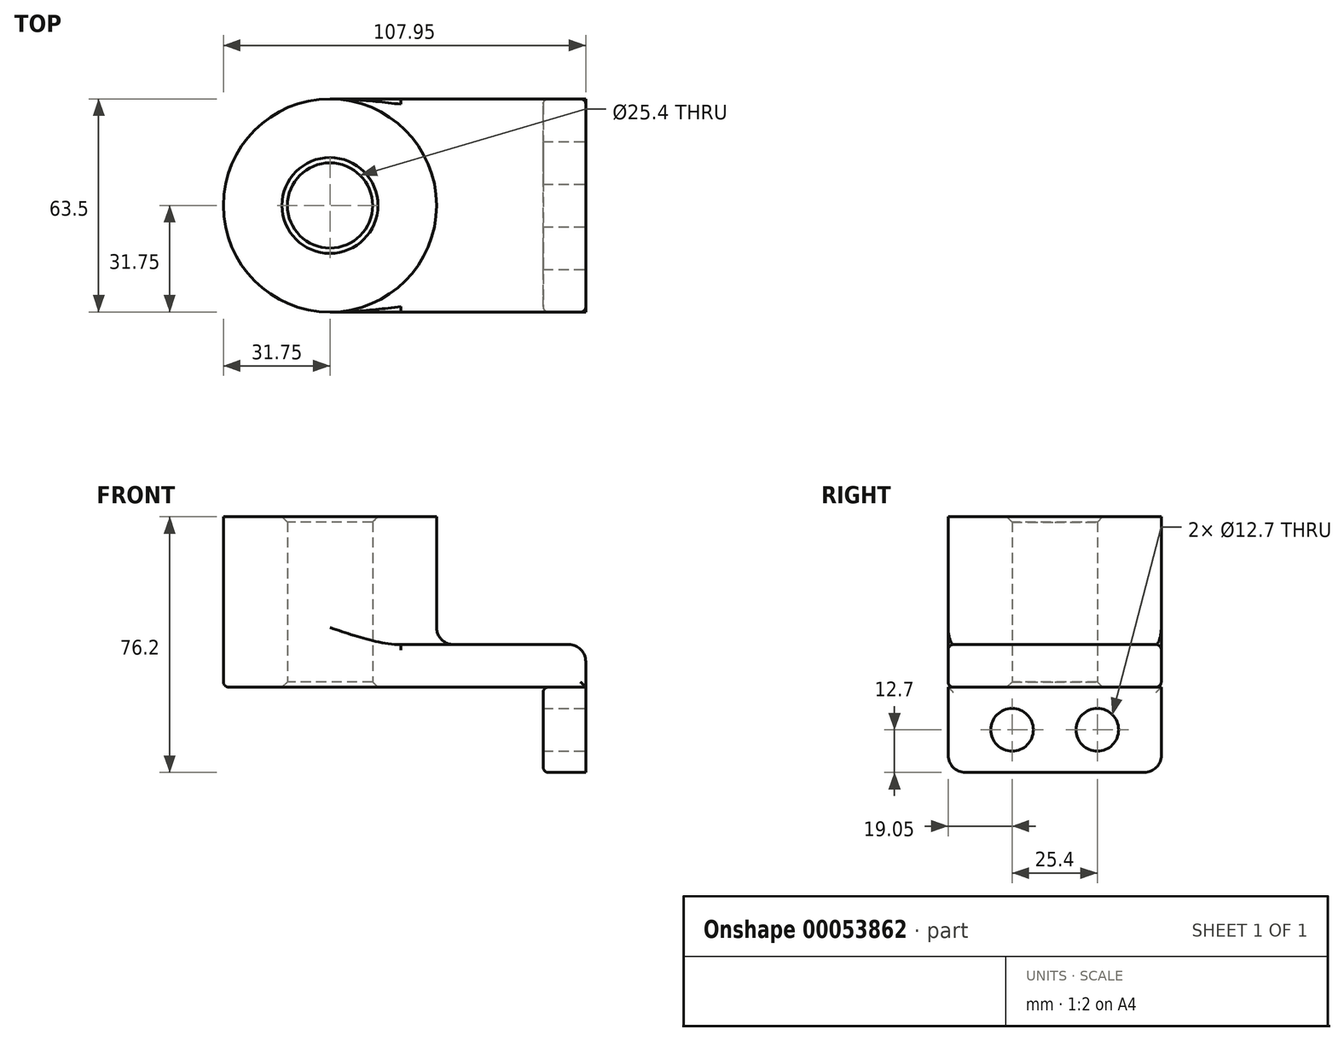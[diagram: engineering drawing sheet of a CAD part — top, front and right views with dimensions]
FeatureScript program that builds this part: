
annotation { "Feature Type Name" : "Feature", "Feature Type Description" : "" }
export const myFeature = defineFeature(function(context is Context, id is Id, definition is map)
    precondition{}
    {
        {
            var Q0;
            Q0=qCreatedBy(makeId("Top.planeOp"),FACE);
            var sketch = newSketch(context, id + "F0", { "sketchPlane" : qUnion([Q0])});
            skLineSegment(sketch, "E0.rect.bottom", {"start": v(-38.1, 31.75) * mm, "end": v(38.1, 31.75) * mm});
            skLineSegment(sketch, "E0.rect.top", {"start": v(-38.1, -31.75) * mm, "end": v(38.1, -31.75) * mm});
            skLineSegment(sketch, "E0.rect.left", {"start": v(-38.1, 31.75) * mm, "end": v(-38.1, -31.75) * mm});
            skLineSegment(sketch, "E0.rect.right", {"start": v(38.1, 31.75) * mm, "end": v(38.1, -31.75) * mm});
            skPoint(sketch, "E0.rect.middle", {"position": v(0, 0) * mm});
            skCircle(sketch, "E1", {"center": v(-38.1, 0) * mm, "radius": 31.75 * mm});
            skCircle(sketch, "E2", {"center": v(-38.1, 0) * mm, "radius": 12.7 * mm});
            skSolve(sketch);
        }
        {
            var Q0;
            Q0 = qSketchRegion(id + "F0", true);
            extrude(context, id + "F1", {"entities" : qUnion([Q0]), "depth" : 12.7 * mm});
        }
        {
            var Q0;
            {var subQ1=sQuery(id+"F0.wireOp",EDGE,"E0.rect.left");var subQ3=sQuery(id+"F0.wireOp",EDGE,"E2");var subQ4=makeQuery(id+"F0.imprint","INTERSECT",VERTEX,{"disambiguationData":[OD(0.0)],"derivedFrom":[subQ1,subQ3]});Q0=makeQuery(id+"F0.imprint","IMPRINT",FACE,{"disambiguationData":[TD([[makeQuery(id+"F0.imprint","IMPRINT",EDGE,{"disambiguationData":[TD([[subQ4,-1.0]])],"derivedFrom":subQ3}),-1.0]])]});}
            var Q1;
            {var subQ1=sQuery(id+"F0.wireOp",EDGE,"E0.rect.left");var subQ3=sQuery(id+"F0.wireOp",EDGE,"E2");var subQ4=makeQuery(id+"F0.imprint","INTERSECT",VERTEX,{"disambiguationData":[OD(0.0)],"derivedFrom":[subQ1,subQ3]});Q1=makeQuery(id+"F0.imprint","IMPRINT",FACE,{"disambiguationData":[TD([[makeQuery(id+"F0.imprint","IMPRINT",EDGE,{"disambiguationData":[TD([[subQ4,1.0]])],"derivedFrom":subQ3}),-1.0]])]});}
            extrude(context, id + "F2", {"entities" : qUnion([Q0, Q1]), "operationType" : NewBodyOperationType.ADD, "depth" : 50.8 * mm});
        }
        {
            var Q0;
            Q0=makeQuery(id+"F1.opExtrude","SWEPT_FACE",FACE,{"disambiguationData":[OSD([sQuery(id+"F0.wireOp",EDGE,"E0.rect.right")])]});
            var sketch = newSketch(context, id + "F3", { "sketchPlane" : qUnion([Q0])});
            skLineSegment(sketch, "E3.bottom", {"start": v(-31.75, 12.7) * mm, "end": v(31.75, 12.7) * mm});
            skLineSegment(sketch, "E3.top", {"start": v(-31.75, -25.4) * mm, "end": v(31.75, -25.4) * mm});
            skLineSegment(sketch, "E3.left", {"start": v(-31.75, 12.7) * mm, "end": v(-31.75, -25.4) * mm});
            skLineSegment(sketch, "E3.right", {"start": v(31.75, 12.7) * mm, "end": v(31.75, -25.4) * mm});
            skCircle(sketch, "E4", {"center": v(-12.7, -12.7) * mm, "radius": 6.35 * mm});
            skLineSegment(sketch, "E5", {"start": v(0, 0) * mm, "end": v(0, -25.4) * mm, "construction": true});
            skCircle(sketch, "E6.MirrorC", {"center": v(12.7, -12.7) * mm, "radius": 6.35 * mm});
            skSolve(sketch);
        }
        {
            var Q0;
            {var subQ2=sQuery(id+"F3.wireOp",EDGE,"E3.top");Q0=makeQuery(id+"F3.imprint","IMPRINT",FACE,{"disambiguationData":[TD([[makeQuery(id+"F3.imprint","IMPRINT",EDGE,{"derivedFrom":subQ2}),1.0]])]});}
            extrude(context, id + "F4", {"entities" : qUnion([Q0]), "oppositeDirection" : true, "depth" : 12.7 * mm});
        }
        {
            var Q0;
            {var subQ0=sQuery(id+"F0.wireOp",EDGE,"E1");Q0=makeQuery(id+"F2.boolean.opBoolean","INTERSECT",EDGE,{"derivedFrom":[makeQuery(id+"F1.opExtrude","CAP_FACE",FACE,{"disambiguationData":[OSD([sQuery(id+"F0.wireOp",EDGE,"E0.rect.bottom"),sQuery(id+"F0.wireOp",EDGE,"E0.rect.top"),sQuery(id+"F0.wireOp",EDGE,"E0.rect.right"),subQ0,sQuery(id+"F0.wireOp",EDGE,"E2")])],"isStart":false}),makeQuery(id+"F2.opExtrude","SWEPT_FACE",FACE,{"disambiguationData":[OSD([subQ0])]})]});}
            var Q1;
            Q1=makeQuery(id+"F1.opExtrude","CAP_EDGE",EDGE,{"disambiguationData":[OSD([sQuery(id+"F0.wireOp",EDGE,"E0.rect.right")])],"isStart":false});
            var Q2;
            Q2=makeQuery(id+"F4.opExtrude","SWEPT_EDGE",EDGE,{"disambiguationData":[OSD([sQuery(id+"F3.wireOp",EDGE,"E3.top"),sQuery(id+"F3.wireOp",EDGE,"E3.left")])]});
            var Q3;
            Q3=makeQuery(id+"F4.opExtrude","SWEPT_EDGE",EDGE,{"disambiguationData":[OSD([sQuery(id+"F3.wireOp",EDGE,"E3.top"),sQuery(id+"F3.wireOp",EDGE,"E3.right")])]});
            fillet(context, id + "F5", {"entities" : qUnion([Q0, Q1, Q2, Q3]), "radius" : 5.08 * mm, "tangentPropagation" : true, "allowEdgeOverflow" : false});
        }
        {
            var Q0;
            Q0=makeQuery(id+"F1.opExtrude","CAP_EDGE",EDGE,{"disambiguationData":[OSD([sQuery(id+"F0.wireOp",EDGE,"E0.rect.top")])],"isStart":true});
            var Q1;
            Q1=makeQuery(id+"F4.opExtrude","CAP_EDGE",EDGE,{"disambiguationData":[OSD([sQuery(id+"F3.wireOp",EDGE,"E3.left")])],"isStart":false});
            var Q2;
            Q2=makeQuery(id+"F1.opExtrude","CAP_EDGE",EDGE,{"disambiguationData":[OSD([sQuery(id+"F0.wireOp",EDGE,"E0.rect.top")])],"isStart":false});
            var Q3;
            Q3=makeQuery(id+"F4.opExtrude","CAP_EDGE",EDGE,{"disambiguationData":[OSD([sQuery(id+"F0.wireOp",EDGE,"E0.rect.right")])],"isStart":false});
            var Q4;
            Q4=makeQuery(id+"F1.opExtrude","CAP_EDGE",EDGE,{"disambiguationData":[OSD([sQuery(id+"F0.wireOp",EDGE,"E0.rect.bottom")])],"isStart":false});
            fillet(context, id + "F6", {"entities" : qUnion([Q0, Q1, Q2, Q3, Q4]), "radius" : 1.59 * mm, "tangentPropagation" : true, "allowEdgeOverflow" : false});
        }
        {
            var Q0;
            {var subQ0=sQuery(id+"F0.wireOp",EDGE,"E2");Q0=makeQuery(id+"F2.boolean.opBoolean","MERGE",FACE,{"derivedFrom":[makeQuery(id+"F1.opExtrude","SWEPT_FACE",FACE,{"disambiguationData":[OSD([subQ0])]}),makeQuery(id+"F2.opExtrude","SWEPT_FACE",FACE,{"disambiguationData":[OSD([subQ0])]})]});}
            chamfer(context, id + "F7", {"entities" : qUnion([Q0]), "width" : 1.59 * mm, "tangentPropagation" : true});
        }
    });
